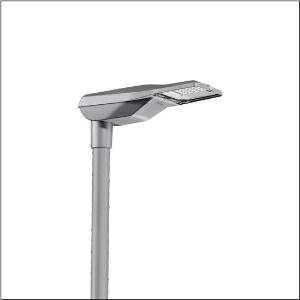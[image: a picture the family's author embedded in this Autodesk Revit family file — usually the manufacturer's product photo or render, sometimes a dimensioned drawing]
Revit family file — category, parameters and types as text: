
# Revit family: streetlight_sl_21_iq_micro___st0_8a_5xe1c41d08db_9d18
name_source: partatom
category: Lighting Fixtures
units: mm (PartAtom-declared; Revit-internal decimal feet)

## family parameters
Cut with Voids When Loaded = No
Host = Face
Light Source = No
Part Type = Normal
Room Calculation Point = No
Round Connector Dimension = Use Diameter
Shared = No

## types (1)
- --- (1 x LED, 5010 lm, 36.4 W, 4000K)
    Apparent Load = 36 VA
    CIE Flux Codes = 38 75 97 100 100
    Color Rendering = 70
    Color Temperature = 4000K
    Default Elevation = 1800 mm
    Description = Streetlight SL 21 iQ micro, mast luminaire, primary light control with lens, of PMMA, primary optical cover: cover, of toughened safety glass, transparent, light distribution: ST0.8a, light emission: direct distribution, primary light characteristic: asymmetric, installation type: post-top, side-entry, LED, High Power LED, rated luminous flux: 5.010lm, luminous efficacy: 138lm/W, light colour: 740, colour temperature: 4000K, control: Auto-Match, Temp-Guard, Lumen-Switch, Night-Set, Smart-Wire, Light-Fading, Desk-Remote (wireless, voltage-free reading and setting of iQ features in the workshop via application-optimized NFC function/RFID function), optimised constant luminous flux control (CLO 2.0), presetting dimming linear, mains connection: 220..240V, AC, 50/60Hz, start of lifetime: 36W, end of service life: 38W, reduction: 16W, luminaire housing, of diecast aluminium, powder-coated, Siteco® metallic grey (DB 702S), corrosivity category C5 mid according to DIN EN ISO 12944, please order mast flange separately, inclination adjustable: 0°, 5°, 10°, 15°, sealing non-destructively replaceable, multi-level sealing system, length: 528mm, width: 235mm, height: 110mm, mast flange for spigot size: 42mm (side-entry): 5XC10008XM4, 60/48mm (side-entry/post-top): 5XC10108XM2, 76/60mm (side-entry/post-top): 5XC10108XM1, protection rating (complete): IP66, insulation class (complete): insulation class II (safety insulation), certification: CE, ENEC, ENEC+, VDE, impact resistance: IK09, permissible operating ambient temperature for outdoor applications: -40..+50°C, standard-compliant lighting for roads and squares, packaging unit: 1 piece

Light Distribution: ST0.8a
    Height = 110 mm
    Lamp = 1 x LED
    Lamp Light Flux = 5010 lm
    Lamp Power = 36.4 W
    Lamp count = 1
    Length = 528 mm
    Luminous efficacy = 138 lm/W
    Manufacturer = Siteco
    ModVariant = No
    Model = 5XE1C41D08DB
    Number of Poles = 1
    OnlyDefault = Yes
    Power Factor = 1
    Product Name = Streetlight SL 21 iQ micro | ST0.8a
    Product group = mast luminaire | pylon top
    ProductGroupID = 6100
    Protection Class = Protection class II
    Protection Degree = IP 66
    RLX_Detail_Level = 1
    RLX_Emergency_Light_Flux = 0 lm
    RLX_Emergency_Type = 0
    RLX_Emergency_Type_DB = No
    RlxData = <blob elided: 99061 chars, md5=fa5dc4f6>
    Socket = socket
    Standby Power = 0 W
    System Light Flux = 5010 lm
    System Power = 36 W
    Type Comments = factory setting: luminous flux: 100 % | dim-lin: 254 | 715 mA
    Type Image = l_1006881.jpg
    URL = http://relux.com
    VarID = @adj_104659
    Voltage = 0 V
    Weight = 0.00 kg
    Width = 235 mm

## geometry (parser evidence)
native form markers: Blend x4, Sweep x10
no freeform markers — native parametric forms only
